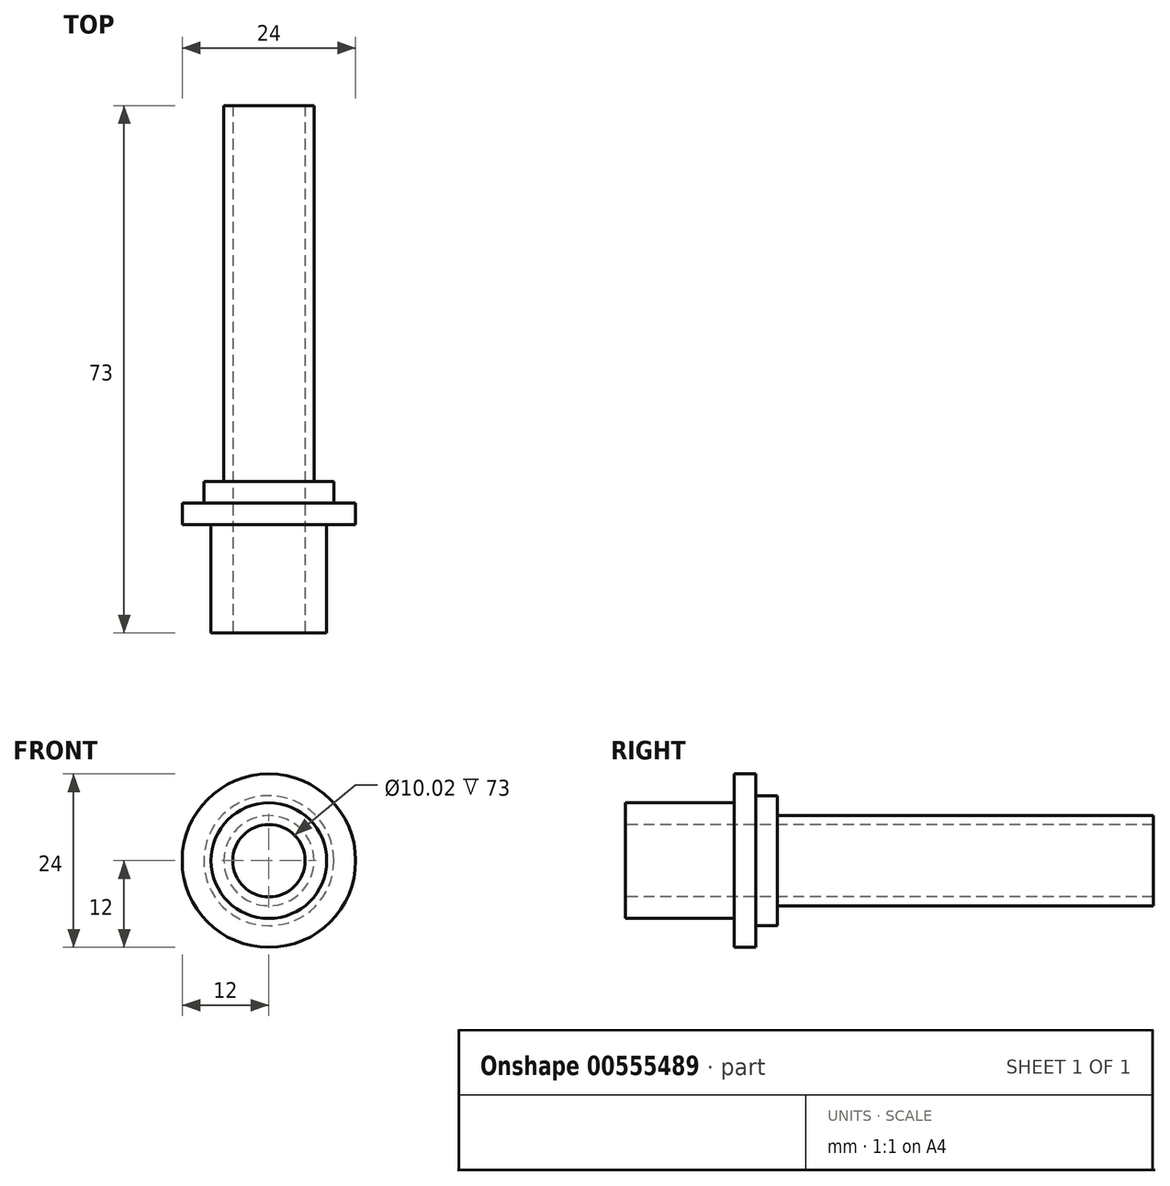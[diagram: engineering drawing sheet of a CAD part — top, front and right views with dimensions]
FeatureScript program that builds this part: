
annotation { "Feature Type Name" : "Feature", "Feature Type Description" : "" }
export const myFeature = defineFeature(function(context is Context, id is Id, definition is map)
    precondition{}
    {
        {
            var Q0;
            Q0=qCreatedBy(makeId("Right.planeOp"),FACE);
            var sketch = newSketch(context, id + "F0", { "sketchPlane" : qUnion([Q0])});
            skLineSegment(sketch, "E0", {"start": v(0, 5) * mm, "end": v(0, 8) * mm});
            skLineSegment(sketch, "E1", {"start": v(0, 8) * mm, "end": v(15, 8) * mm});
            skLineSegment(sketch, "E2", {"start": v(15, 8) * mm, "end": v(15, 12) * mm});
            skLineSegment(sketch, "E3", {"start": v(15, 12) * mm, "end": v(18, 12) * mm});
            skLineSegment(sketch, "E4", {"start": v(18, 12) * mm, "end": v(18, 9) * mm});
            skLineSegment(sketch, "E5", {"start": v(21, 6.23) * mm, "end": v(73, 6.23) * mm});
            skLineSegment(sketch, "E6", {"start": v(73, 6.23) * mm, "end": v(73, 5.01) * mm});
            skLineSegment(sketch, "E7", {"start": v(73, 5.01) * mm, "end": v(0, 5) * mm});
            skLineSegment(sketch, "E8", {"start": v(0, 0) * mm, "end": v(55.93, 0) * mm});
            skLineSegment(sketch, "E9", {"start": v(21, 6.23) * mm, "end": v(21, 9) * mm});
            skLineSegment(sketch, "E10", {"start": v(21, 9) * mm, "end": v(18, 9) * mm});
            skSolve(sketch);
        }
        {
            var Q0;
            Q0 = qSketchRegion(id + "F0", true);
            var Q1;
            Q1=sQuery(id+"F0.wireOp",EDGE,"E8");
            revolve(context, id + "F1", {"entities" : qUnion([Q0]), "axis" : qUnion([Q1]), "revolveType" : RevolveType.FULL});
        }
    });
